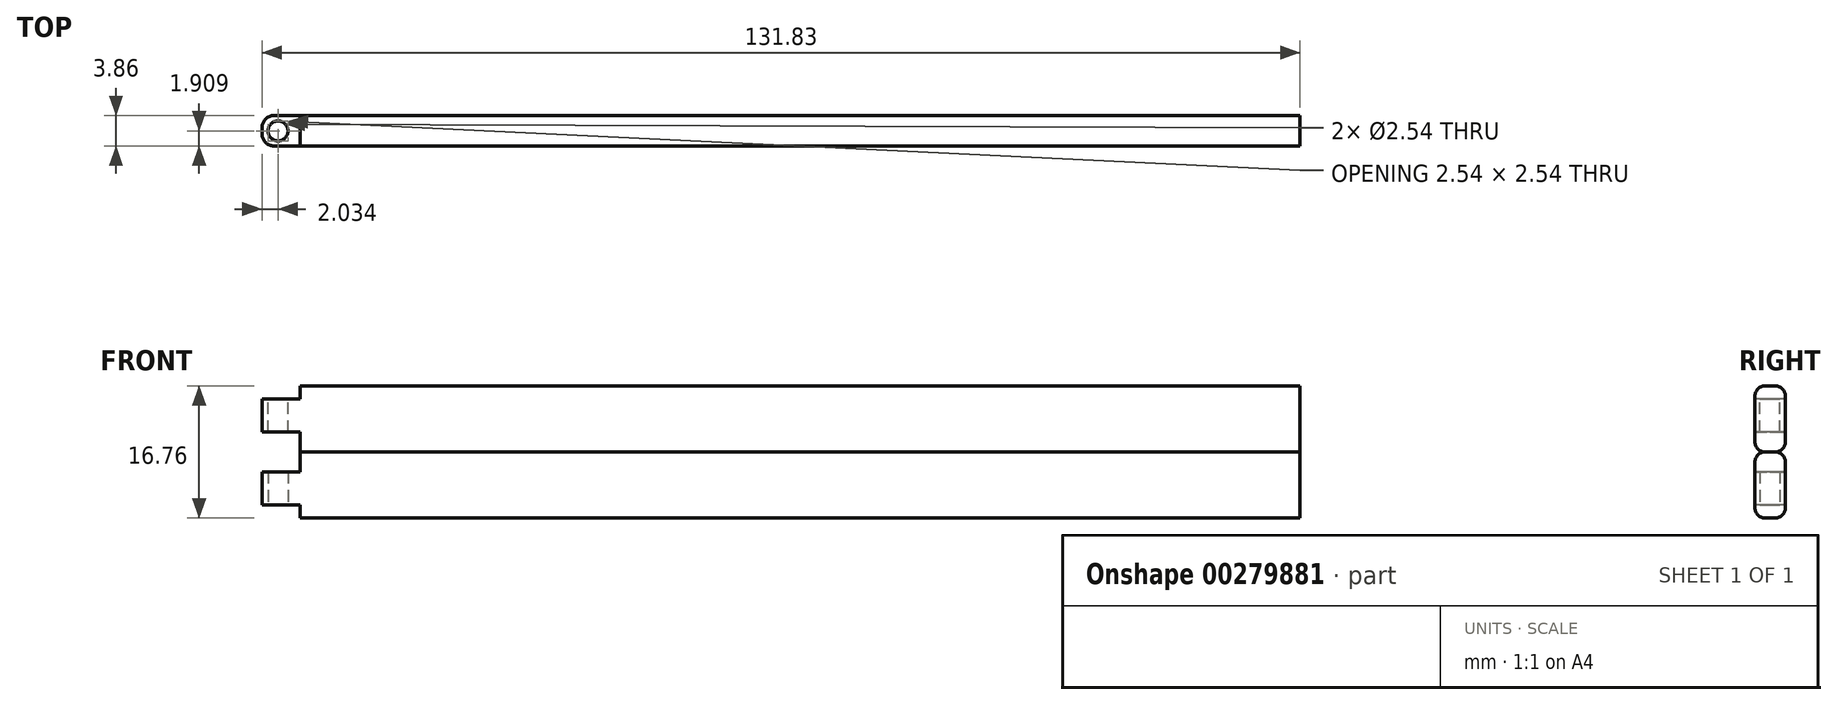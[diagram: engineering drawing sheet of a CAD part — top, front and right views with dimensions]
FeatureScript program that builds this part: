
annotation { "Feature Type Name" : "Feature", "Feature Type Description" : "" }
export const myFeature = defineFeature(function(context is Context, id is Id, definition is map)
    precondition{}
    {
        {
            var Q0;
            Q0=qCreatedBy(makeId("Front.planeOp"),FACE);
            var sketch = newSketch(context, id + "F0", { "sketchPlane" : qUnion([Q0])});
            skLineSegment(sketch, "E0", {"start": v(-54.83, 8.38) * mm, "end": v(-54.83, 0) * mm});
            skLineSegment(sketch, "E1", {"start": v(-54.83, 0) * mm, "end": v(72.17, 0) * mm});
            skLineSegment(sketch, "E2", {"start": v(72.17, 0) * mm, "end": v(72.17, 8.38) * mm});
            skLineSegment(sketch, "E3", {"start": v(72.17, 8.38) * mm, "end": v(-54.83, 8.38) * mm});
            skSolve(sketch);
        }
        {
            var Q0;
            Q0 = qSketchRegion(id + "F0", true);
            extrude(context, id + "F1", {"entities" : qUnion([Q0]), "depth" : 3.86 * mm});
        }
        {
            var Q0;
            Q0=makeQuery(id+"F1.opExtrude","CAP_FACE",FACE,{"disambiguationData":[OSD([sQuery(id+"F0.wireOp",EDGE,"E0"),sQuery(id+"F0.wireOp",EDGE,"E1"),sQuery(id+"F0.wireOp",EDGE,"E2"),sQuery(id+"F0.wireOp",EDGE,"E3")])],"isStart":false});
            var sketch = newSketch(context, id + "F2", { "sketchPlane" : qUnion([Q0])});
            skLineSegment(sketch, "E4", {"start": v(-54.83, 6.7) * mm, "end": v(-59.66, 6.7) * mm});
            skLineSegment(sketch, "E5", {"start": v(-59.66, 6.7) * mm, "end": v(-59.66, 2.52) * mm});
            skLineSegment(sketch, "E6", {"start": v(-59.66, 2.52) * mm, "end": v(-54.83, 2.52) * mm});
            skLineSegment(sketch, "E7", {"start": v(-54.83, 8.38) * mm, "end": v(-59.44, 8.38) * mm});
            skSolve(sketch);
        }
        {
            var Q0;
            {var subQ0=sQuery(id+"F2.wireOp",EDGE,"E4");Q0=makeQuery(id+"F2.imprint","IMPRINT",FACE,{"disambiguationData":[TD([[makeQuery(id+"F2.imprint","IMPRINT",EDGE,{"derivedFrom":subQ0}),1.0]])]});}
            extrude(context, id + "F3", {"entities" : qUnion([Q0]), "operationType" : NewBodyOperationType.ADD, "oppositeDirection" : true, "depth" : 3.86 * mm});
        }
        {
            var Q0;
            Q0=makeQuery(id+"F3.opExtrude","SWEPT_FACE",FACE,{"disambiguationData":[OSD([sQuery(id+"F2.wireOp",EDGE,"E4")])]});
            var sketch = newSketch(context, id + "F4", { "sketchPlane" : qUnion([Q0])});
            skCircle(sketch, "E8", {"center": v(-57.63, -1.95) * mm, "radius": 1.27 * mm});
            skSolve(sketch);
        }
        {
            var Q0;
            Q0 = qSketchRegion(id + "F4", true);
            extrude(context, id + "F5", {"entities" : qUnion([Q0]), "operationType" : NewBodyOperationType.REMOVE, "endBound" : BoundingType.THROUGH_ALL, "oppositeDirection" : true, "depth" : 25.4 * mm});
        }
        {
            var Q0;
            Q0=makeQuery(id+"F1.opExtrude","CAP_EDGE",EDGE,{"disambiguationData":[OSD([sQuery(id+"F0.wireOp",EDGE,"E3")])],"isStart":false});
            var Q1;
            Q1=makeQuery(id+"F1.opExtrude","CAP_EDGE",EDGE,{"disambiguationData":[OSD([sQuery(id+"F0.wireOp",EDGE,"E3")])],"isStart":true});
            var Q2;
            Q2=makeQuery(id+"F1.opExtrude","CAP_EDGE",EDGE,{"disambiguationData":[OSD([sQuery(id+"F0.wireOp",EDGE,"E1")])],"isStart":false});
            var Q3;
            Q3=makeQuery(id+"F1.opExtrude","CAP_EDGE",EDGE,{"disambiguationData":[OSD([sQuery(id+"F0.wireOp",EDGE,"E1")])],"isStart":true});
            fillet(context, id + "F6", {"entities" : qUnion([Q0, Q1, Q2, Q3]), "radius" : 1.27 * mm, "tangentPropagation" : true, "allowEdgeOverflow" : false});
        }
        {
            var Q0;
            Q0=makeQuery(id+"F3.opExtrude","CAP_EDGE",EDGE,{"disambiguationData":[OSD([sQuery(id+"F2.wireOp",EDGE,"E5")])],"isStart":true});
            var Q1;
            Q1=makeQuery(id+"F3.opExtrude","CAP_EDGE",EDGE,{"disambiguationData":[OSD([sQuery(id+"F2.wireOp",EDGE,"E5")])],"isStart":false});
            fillet(context, id + "F7", {"entities" : qUnion([Q0, Q1]), "radius" : 1.52 * mm, "tangentPropagation" : true, "allowEdgeOverflow" : false});
        }
        {
            var Q0;
            Q0=makeQuery(id+"F1.opExtrude","SWEPT_BODY",BODY,{"disambiguationData":[OSD([sQuery(id+"F0.wireOp",EDGE,"E0"),sQuery(id+"F0.wireOp",EDGE,"E1"),sQuery(id+"F0.wireOp",EDGE,"E2"),sQuery(id+"F0.wireOp",EDGE,"E3")])]});
            var Q1;
            Q1=qCreatedBy(makeId("Top.planeOp"),FACE);
            mirror(context, id + "F8", {"entities" : qUnion([Q0]), "mirrorPlane" : qUnion([Q1])});
        }
    });
